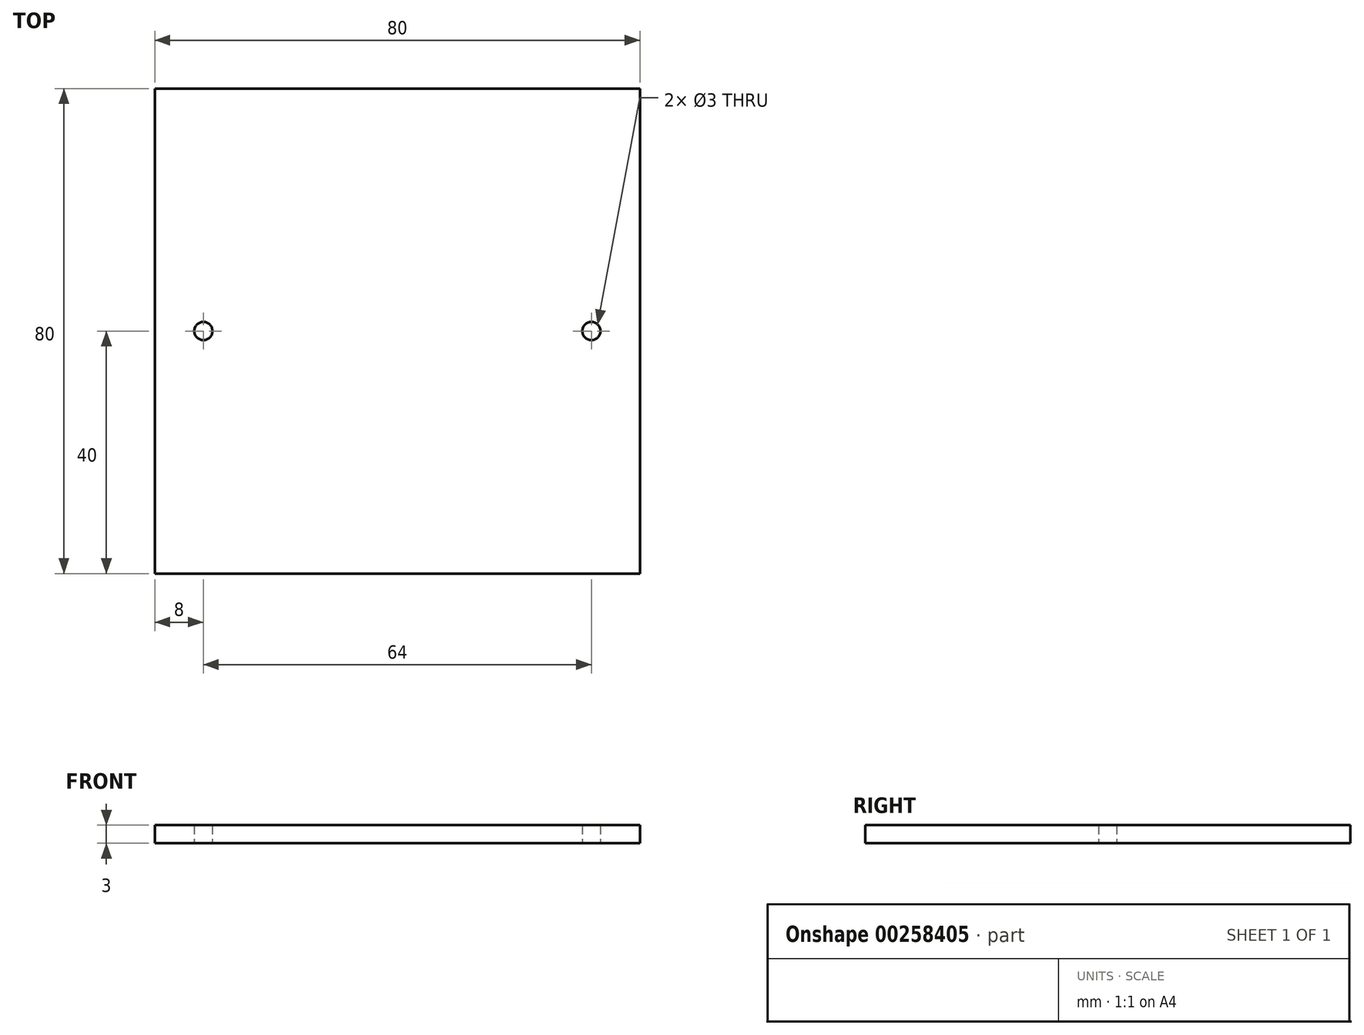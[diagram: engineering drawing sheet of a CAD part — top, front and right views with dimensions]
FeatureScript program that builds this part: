
annotation { "Feature Type Name" : "Feature", "Feature Type Description" : "" }
export const myFeature = defineFeature(function(context is Context, id is Id, definition is map)
    precondition{}
    {
        {
            var Q0;
            Q0=qCreatedBy(makeId("Top.planeOp"),FACE);
            var sketch = newSketch(context, id + "F0", { "sketchPlane" : qUnion([Q0])});
            skLineSegment(sketch, "E0.bottom", {"start": v(40, -40) * mm, "end": v(-40, -40) * mm});
            skLineSegment(sketch, "E0.top", {"start": v(40, 40) * mm, "end": v(-40, 40) * mm});
            skLineSegment(sketch, "E0.left", {"start": v(40, -40) * mm, "end": v(40, 40) * mm});
            skLineSegment(sketch, "E0.right", {"start": v(-40, -40) * mm, "end": v(-40, 40) * mm});
            skPoint(sketch, "E0.middle", {"position": v(0, 0) * mm});
            skCircle(sketch, "E1", {"center": v(-32, 0) * mm, "radius": 1.5 * mm});
            skCircle(sketch, "E2.MirrorC", {"center": v(32, 0) * mm, "radius": 1.5 * mm});
            skSolve(sketch);
        }
        {
            var Q0;
            Q0=makeQuery(id+"F0.imprint","IMPRINT",FACE,{"disambiguationData":[TD([[makeQuery(id+"F0.imprint","IMPRINT",EDGE,{"derivedFrom":sQuery(id+"F0.wireOp",EDGE,"E0.bottom")}),-1.0]])]});
            extrude(context, id + "F1", {"entities" : qUnion([Q0]), "depth" : 3 * mm});
        }
    });
